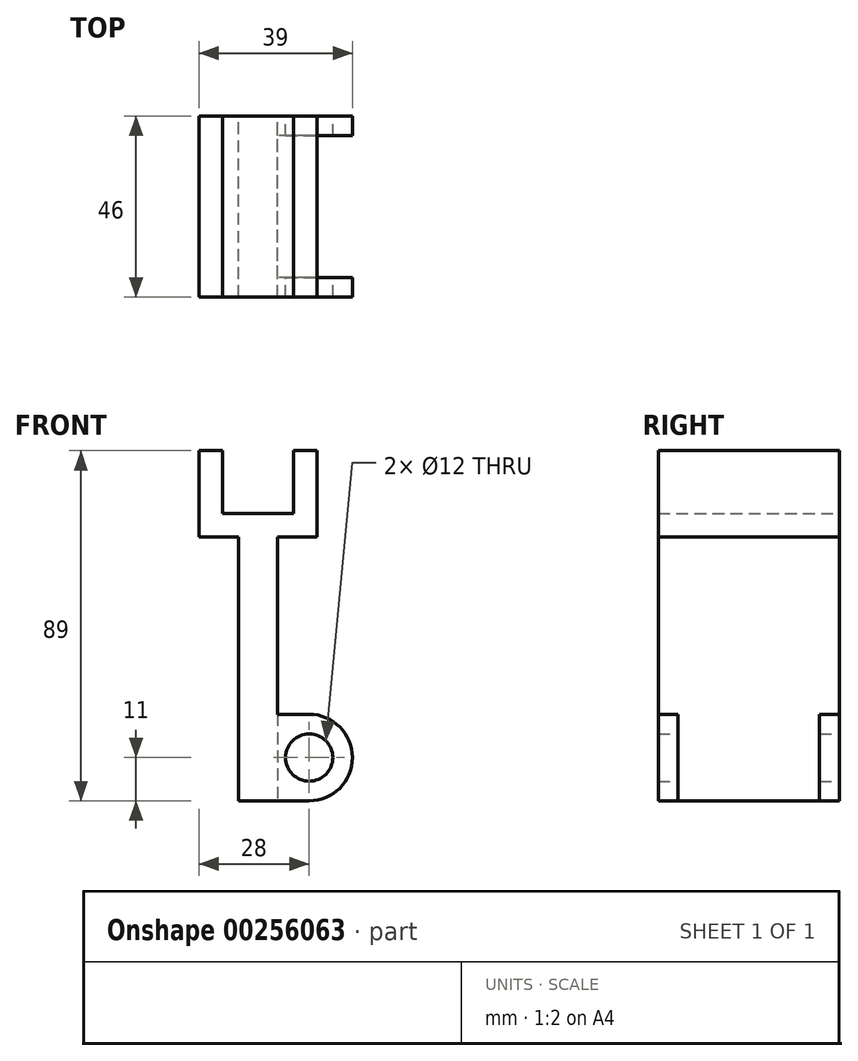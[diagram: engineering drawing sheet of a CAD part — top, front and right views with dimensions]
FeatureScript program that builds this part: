
annotation { "Feature Type Name" : "Feature", "Feature Type Description" : "" }
export const myFeature = defineFeature(function(context is Context, id is Id, definition is map)
    precondition{}
    {
        {
            var Q0;
            Q0=qCreatedBy(makeId("Front.planeOp"),FACE);
            var sketch = newSketch(context, id + "F0", { "sketchPlane" : qUnion([Q0])});
            skLineSegment(sketch, "E0", {"start": v(0, 10.67) * mm, "end": v(0, -24.52) * mm, "construction": true});
            skLineSegment(sketch, "E1", {"start": v(5, 0) * mm, "end": v(15, 0) * mm});
            skLineSegment(sketch, "E2", {"start": v(15, 0) * mm, "end": v(15, 22) * mm});
            skLineSegment(sketch, "E3", {"start": v(15, 22) * mm, "end": v(9, 22) * mm});
            skLineSegment(sketch, "E4", {"start": v(9, 22) * mm, "end": v(9, 6) * mm});
            skLineSegment(sketch, "E5", {"start": v(9, 6) * mm, "end": v(0, 6) * mm});
            skLineSegment(sketch, "E6", {"start": v(15, 0) * mm, "end": v(5, 0) * mm, "construction": true});
            skLineSegment(sketch, "E7", {"start": v(5, 0) * mm, "end": v(5, -45) * mm});
            skLineSegment(sketch, "E8.MirrorCS", {"start": v(-9, 6) * mm, "end": v(0, 6) * mm});
            skLineSegment(sketch, "E9.MirrorCS", {"start": v(-9, 22) * mm, "end": v(-9, 6) * mm});
            skLineSegment(sketch, "E10.MirrorCS", {"start": v(-15, 22) * mm, "end": v(-9, 22) * mm});
            skLineSegment(sketch, "E11.MirrorCS", {"start": v(-15, 0) * mm, "end": v(-15, 22) * mm});
            skLineSegment(sketch, "E12.MirrorCS", {"start": v(-5, 0) * mm, "end": v(-15, 0) * mm});
            skLineSegment(sketch, "E13.MirrorCS", {"start": v(-5, 0) * mm, "end": v(-5, -67) * mm});
            skLineSegment(sketch, "E14", {"start": v(-5, -67) * mm, "end": v(5, -67) * mm});
            skArc(sketch, "E15", {"start": v(13, -67) * mm, "mid": v(24, -56) * mm, "end": v(13, -45) * mm});
            skCircle(sketch, "E16", {"center": v(13, -56) * mm, "radius": 6 * mm});
            skLineSegment(sketch, "E17", {"start": v(13, -45) * mm, "end": v(5, -45) * mm});
            skLineSegment(sketch, "E18", {"start": v(13, -67) * mm, "end": v(5, -67) * mm});
            skSolve(sketch);
        }
        {
            var Q0;
            Q0=makeQuery(id+"F0.imprint","IMPRINT",FACE,{"disambiguationData":[TD([[makeQuery(id+"F0.imprint","IMPRINT",EDGE,{"derivedFrom":sQuery(id+"F0.wireOp",EDGE,"E1")}),1.0]])]});
            extrude(context, id + "F1", {"entities" : qUnion([Q0]), "depth" : 46 * mm});
        }
        {
            var Q0;
            Q0=makeQuery(id+"F1.opExtrude","SWEPT_FACE",FACE,{"disambiguationData":[OSD([sQuery(id+"F0.wireOp",EDGE,"E7")])]});
            var sketch = newSketch(context, id + "F2", { "sketchPlane" : qUnion([Q0])});
            skLineSegment(sketch, "E19", {"start": v(-46, -45) * mm, "end": v(-41, -45) * mm, "construction": true});
            skLineSegment(sketch, "E20", {"start": v(-41, -45) * mm, "end": v(-41, -73.49) * mm});
            skLineSegment(sketch, "E21", {"start": v(-41, -73.49) * mm, "end": v(-5, -73.49) * mm});
            skLineSegment(sketch, "E22", {"start": v(-5, -73.49) * mm, "end": v(-5, -45) * mm});
            skLineSegment(sketch, "E23", {"start": v(-5, -45) * mm, "end": v(-41, -45) * mm});
            skSolve(sketch);
        }
        {
            var Q0;
            Q0=makeQuery(id+"F2.imprint","IMPRINT",FACE,{"disambiguationData":[TD([[makeQuery(id+"F2.imprint","IMPRINT",EDGE,{"derivedFrom":sQuery(id+"F2.wireOp",EDGE,"E20")}),1.0]])]});
            extrude(context, id + "F3", {"entities" : qUnion([Q0]), "depth" : 25 * mm});
        }
        {
            var Q0;
            Q0=makeQuery(id+"F3.opExtrude","SWEPT_BODY",BODY,{"disambiguationData":[OSD([sQuery(id+"F2.wireOp",EDGE,"E20"),sQuery(id+"F2.wireOp",EDGE,"E21"),sQuery(id+"F2.wireOp",EDGE,"E22"),sQuery(id+"F2.wireOp",EDGE,"E23")])]});
            var Q1;
            Q1=makeQuery(id+"F1.opExtrude","SWEPT_BODY",BODY,{"disambiguationData":[OSD([sQuery(id+"F0.wireOp",EDGE,"E1"),sQuery(id+"F0.wireOp",EDGE,"E2"),sQuery(id+"F0.wireOp",EDGE,"E3"),sQuery(id+"F0.wireOp",EDGE,"E4"),sQuery(id+"F0.wireOp",EDGE,"E5"),sQuery(id+"F0.wireOp",EDGE,"E7"),sQuery(id+"F0.wireOp",EDGE,"E8.MirrorCS"),sQuery(id+"F0.wireOp",EDGE,"E9.MirrorCS"),sQuery(id+"F0.wireOp",EDGE,"E10.MirrorCS"),sQuery(id+"F0.wireOp",EDGE,"E11.MirrorCS"),sQuery(id+"F0.wireOp",EDGE,"E12.MirrorCS"),sQuery(id+"F0.wireOp",EDGE,"E13.MirrorCS"),sQuery(id+"F0.wireOp",EDGE,"E14"),sQuery(id+"F0.wireOp",EDGE,"E15"),sQuery(id+"F0.wireOp",EDGE,"E16"),sQuery(id+"F0.wireOp",EDGE,"E17"),sQuery(id+"F0.wireOp",EDGE,"E18")])]});
            booleanBodies(context, id + "F4", {"operationType" : BooleanOperationType.SUBTRACTION, "tools" : qUnion([Q0]), "targets" : qUnion([Q1])});
        }
    });
